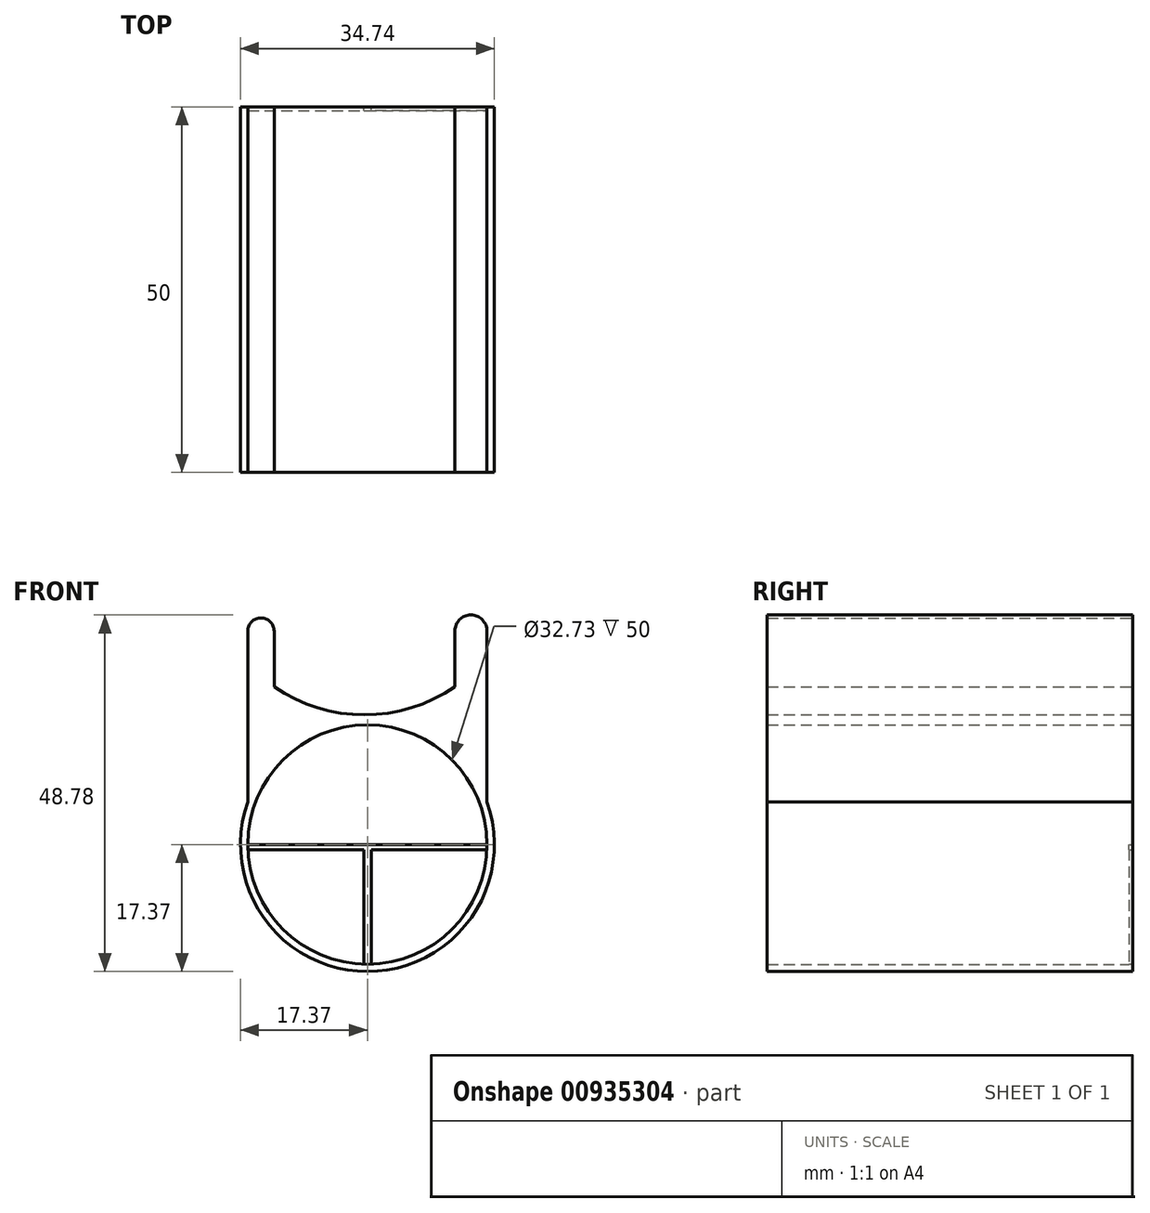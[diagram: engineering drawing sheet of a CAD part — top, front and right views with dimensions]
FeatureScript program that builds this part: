
annotation { "Feature Type Name" : "Feature", "Feature Type Description" : "" }
export const myFeature = defineFeature(function(context is Context, id is Id, definition is map)
    precondition{}
    {
        {
            var Q0;
            Q0=qCreatedBy(makeId("Front.planeOp"),FACE);
            var sketch = newSketch(context, id + "F0", { "sketchPlane" : qUnion([Q0])});
            skCircle(sketch, "E0", {"center": v(0, 0) * mm, "radius": 16.37 * mm});
            skLineSegment(sketch, "E1", {"start": v(0, -16.37) * mm, "end": v(0, 0) * mm});
            skLineSegment(sketch, "E2", {"start": v(-16.37, 0) * mm, "end": v(0, 0) * mm});
            skLineSegment(sketch, "E3", {"start": v(0, 0) * mm, "end": v(16.37, 0) * mm});
            skLineSegment(sketch, "E4", {"start": v(-16.37, 0) * mm, "end": v(-16.37, 29.2) * mm});
            skArc(sketch, "E5", {"start": v(-12.77, 29.2) * mm, "mid": v(-14.57, 31) * mm, "end": v(-16.37, 29.2) * mm});
            skLineSegment(sketch, "E6", {"start": v(-12.77, 29.2) * mm, "end": v(-12.77, 21.57) * mm});
            skLineSegment(sketch, "E7", {"start": v(16.37, 0) * mm, "end": v(16.37, 29.2) * mm});
            skArc(sketch, "E8", {"start": v(16.37, 29.2) * mm, "mid": v(14.16, 31.4) * mm, "end": v(11.96, 29.2) * mm});
            skLineSegment(sketch, "E9", {"start": v(11.96, 29.2) * mm, "end": v(11.96, 21.57) * mm});
            skArc(sketch, "E10", {"start": v(-12.77, 21.57) * mm, "mid": v(-0.4, 17.75) * mm, "end": v(11.96, 21.57) * mm});
            skCircle(sketch, "E11.0", {"center": v(0, 0) * mm, "radius": 17.37 * mm});
            skLineSegment(sketch, "E12", {"start": v(-16.35, -0.69) * mm, "end": v(-0.5, -0.69) * mm});
            skLineSegment(sketch, "E13", {"start": v(-0.5, -0.69) * mm, "end": v(-0.5, -16.36) * mm});
            skLineSegment(sketch, "E14", {"start": v(16.35, -0.69) * mm, "end": v(0.5, -0.69) * mm});
            skLineSegment(sketch, "E15", {"start": v(0.5, -0.69) * mm, "end": v(0.5, -16.36) * mm});
            skSolve(sketch);
        }
        {
            var Q0;
            {var subQ4=sQuery(id+"F0.wireOp",EDGE,"E5");Q0=makeQuery(id+"F0.imprint","IMPRINT",FACE,{"disambiguationData":[TD([[makeQuery(id+"F0.imprint","IMPRINT",EDGE,{"derivedFrom":subQ4}),1.0]])]});}
            var Q1;
            {var subQ0=sQuery(id+"F0.wireOp",EDGE,"E4");var subQ5=sQuery(id+"F0.wireOp",EDGE,"E11.0");var subQ6=makeQuery(id+"F0.imprint","INTERSECT",VERTEX,{"derivedFrom":[subQ0,subQ5]});Q1=makeQuery(id+"F0.imprint","IMPRINT",FACE,{"disambiguationData":[TD([[makeQuery(id+"F0.imprint","IMPRINT",EDGE,{"disambiguationData":[TD([[subQ6,1.0]])],"derivedFrom":subQ5}),1.0]])]});}
            var Q2;
            {var subQ0=sQuery(id+"F0.wireOp",EDGE,"E0");var subQ8=makeQuery(id+"F0.imprint","INTERSECT",VERTEX,{"derivedFrom":[subQ0,sQuery(id+"F0.wireOp",EDGE,"E12")]});Q2=makeQuery(id+"F0.imprint","IMPRINT",FACE,{"disambiguationData":[TD([[makeQuery(id+"F0.imprint","IMPRINT",EDGE,{"disambiguationData":[TD([[subQ8,-1.0]])],"derivedFrom":subQ0}),-1.0]])]});}
            extrude(context, id + "F1", {"entities" : qUnion([Q0, Q1, Q2]), "depth" : 50 * mm, "offsetDistance" : 25 * mm});
        }
        {
            var Q0;
            {var subQ0=sQuery(id+"F0.wireOp",EDGE,"E1");Q0=makeQuery(id+"F0.imprint","IMPRINT",FACE,{"disambiguationData":[TD([[makeQuery(id+"F0.imprint","IMPRINT",EDGE,{"derivedFrom":subQ0}),1.0]])]});}
            var Q1;
            {var subQ0=sQuery(id+"F0.wireOp",EDGE,"E1");Q1=makeQuery(id+"F0.imprint","IMPRINT",FACE,{"disambiguationData":[TD([[makeQuery(id+"F0.imprint","IMPRINT",EDGE,{"derivedFrom":subQ0}),-1.0]])]});}
            extrude(context, id + "F2", {"entities" : qUnion([Q0, Q1]), "operationType" : NewBodyOperationType.ADD, "depth" : .5 * mm, "offsetDistance" : 25 * mm});
        }
    });
